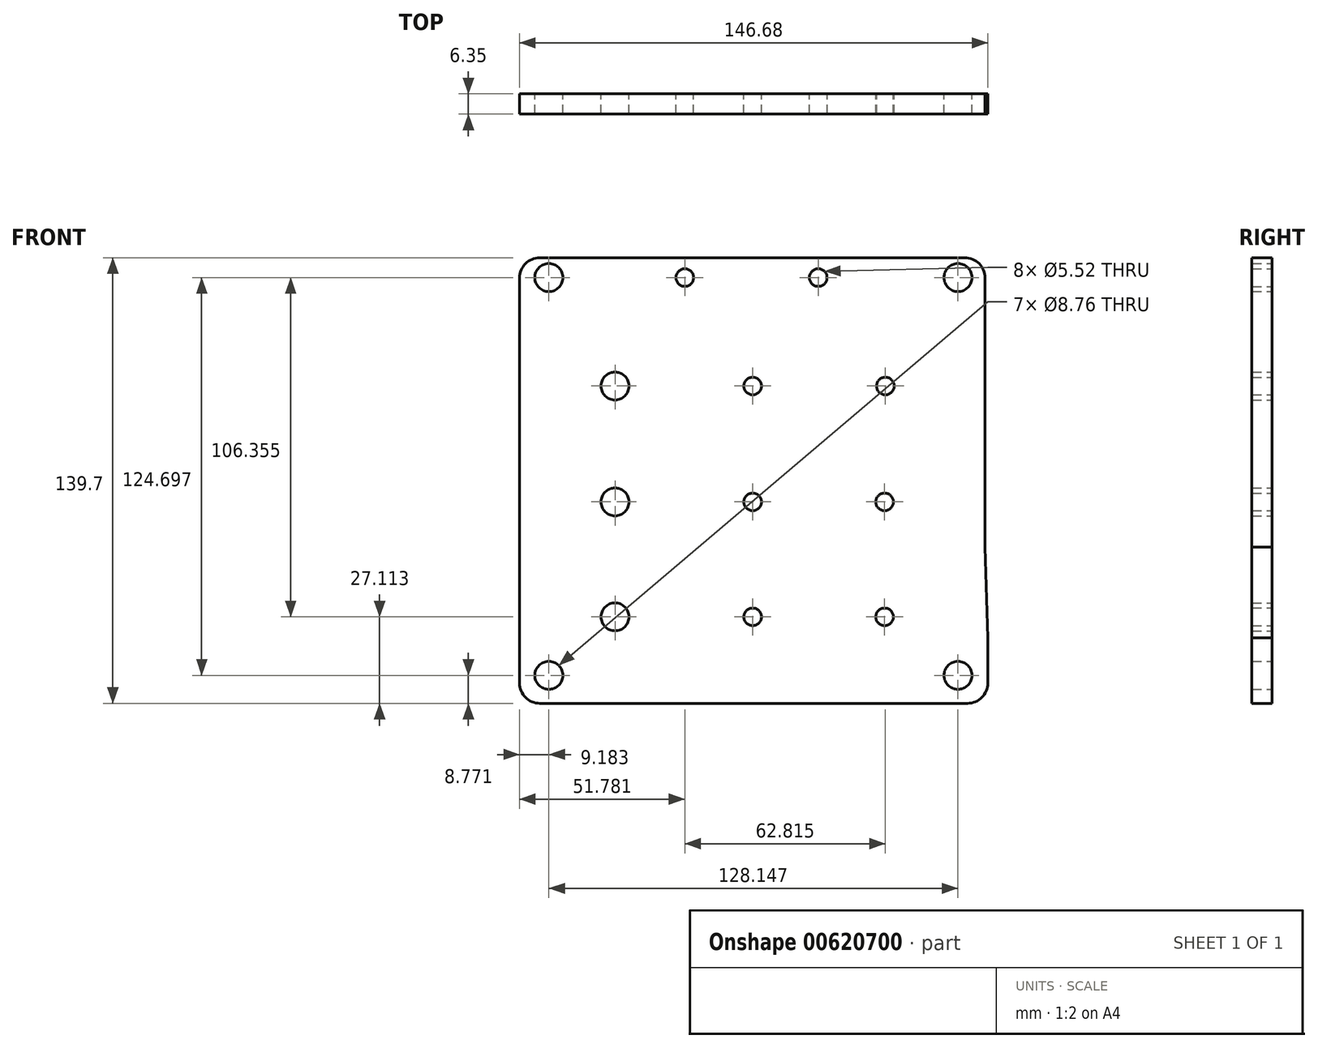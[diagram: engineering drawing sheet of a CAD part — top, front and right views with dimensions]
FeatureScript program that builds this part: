
annotation { "Feature Type Name" : "Feature", "Feature Type Description" : "" }
export const myFeature = defineFeature(function(context is Context, id is Id, definition is map)
    precondition{}
    {
        {
            var Q0;
            Q0=qCreatedBy(makeId("Front.planeOp"),FACE);
            var sketch = newSketch(context, id + "F0", { "sketchPlane" : qUnion([Q0])});
            skLineSegment(sketch, "E0.bottom", {"start": v(66.45, 76.55) * mm, "end": v(-66.69, 76.55) * mm});
            skLineSegment(sketch, "E0.top", {"start": v(67.3, -63.15) * mm, "end": v(-66.69, -63.15) * mm});
            skPoint(sketch, "E0.middle", {"position": v(0, 0) * mm});
            skLineSegment(sketch, "E1", {"start": v(73.64, -56.8) * mm, "end": v(73.64, -42.59) * mm});
            skLineSegment(sketch, "E2", {"start": v(-73.04, -56.8) * mm, "end": v(-73.04, -42.6) * mm});
            skCircle(sketch, "E3", {"center": v(-63.86, 70.32) * mm, "radius": 4.38 * mm});
            skCircle(sketch, "E4", {"center": v(64.3, 70.32) * mm, "radius": 4.38 * mm});
            skCircle(sketch, "E5", {"center": v(-63.86, -54.38) * mm, "radius": 4.38 * mm});
            skCircle(sketch, "E6", {"center": v(64.3, -54.38) * mm, "radius": 4.38 * mm});
            skLineSegment(sketch, "E7", {"start": v(72.8, -14.15) * mm, "end": v(73.64, -42.59) * mm});
            skCircle(sketch, "E8", {"center": v(0, 36.33) * mm, "radius": 2.76 * mm});
            skCircle(sketch, "E9", {"center": v(0, 0) * mm, "radius": 2.76 * mm});
            skCircle(sketch, "E10", {"center": v(0, -36.04) * mm, "radius": 2.76 * mm});
            skCircle(sketch, "E11", {"center": v(-43.13, 36.33) * mm, "radius": 4.38 * mm});
            skCircle(sketch, "E12", {"center": v(-43.13, 0) * mm, "radius": 4.38 * mm});
            skCircle(sketch, "E13", {"center": v(-43.13, -36.04) * mm, "radius": 4.38 * mm});
            skCircle(sketch, "E14", {"center": v(41.56, 36.33) * mm, "radius": 2.76 * mm});
            skCircle(sketch, "E15", {"center": v(41.31, 0) * mm, "radius": 2.76 * mm});
            skCircle(sketch, "E16", {"center": v(41.31, -36.04) * mm, "radius": 2.76 * mm});
            skCircle(sketch, "E17", {"center": v(-21.26, 70.32) * mm, "radius": 2.76 * mm});
            skCircle(sketch, "E18", {"center": v(20.53, 70.32) * mm, "radius": 2.76 * mm});
            skLineSegment(sketch, "E19", {"start": v(-73.04, 70.2) * mm, "end": v(-73.04, -14.15) * mm});
            skLineSegment(sketch, "E20", {"start": v(72.8, 70.2) * mm, "end": v(72.8, -14.15) * mm});
            skLineSegment(sketch, "E21", {"start": v(-73.04, -14.15) * mm, "end": v(-73.04, -42.6) * mm});
            skPoint(sketch, "E22.visualSharp", {"position": v(-73.04, 76.55) * mm});
            skArc(sketch, "E22.filletArc", {"start": v(-66.69, 76.55) * mm, "mid": v(-71.18, 74.7) * mm, "end": v(-73.04, 70.2) * mm});
            skPoint(sketch, "E23.visualSharp", {"position": v(72.8, 76.55) * mm});
            skArc(sketch, "E23.filletArc", {"start": v(72.8, 70.2) * mm, "mid": v(70.94, 74.7) * mm, "end": v(66.45, 76.55) * mm});
            skPoint(sketch, "E24.visualSharp", {"position": v(-73.04, -63.15) * mm});
            skArc(sketch, "E24.filletArc", {"start": v(-73.04, -56.8) * mm, "mid": v(-71.18, -61.29) * mm, "end": v(-66.69, -63.15) * mm});
            skPoint(sketch, "E25.visualSharp", {"position": v(73.64, -63.15) * mm});
            skArc(sketch, "E25.filletArc", {"start": v(67.3, -63.15) * mm, "mid": v(71.78, -61.29) * mm, "end": v(73.64, -56.8) * mm});
            skPoint(sketch, "E26.middle", {"position": v(0, 58.92) * mm});
            skSolve(sketch);
        }
        {
            var Q0;
            Q0=makeQuery(id+"F0.imprint","IMPRINT",FACE,{"disambiguationData":[TD([[makeQuery(id+"F0.imprint","IMPRINT",EDGE,{"derivedFrom":sQuery(id+"F0.wireOp",EDGE,"E0.top")}),-1.0]])]});
            var Q1;
            {var subQ1=sQuery(id+"F0.wireOp",EDGE,"xHYsXOlC-izls-CHSO-2wEK-ZJGDBLUUB7SF");Q1=makeQuery(id+"F0.imprint","IMPRINT",FACE,{"disambiguationData":[TD([[makeQuery(id+"F0.imprint","IMPRINT",EDGE,{"derivedFrom":subQ1}),-1.0]])]});}
            extrude(context, id + "F1", {"entities" : qUnion([Q0, Q1]), "depth" : 6.35 * mm, "offsetDistance" : 25.4 * mm});
        }
    });
